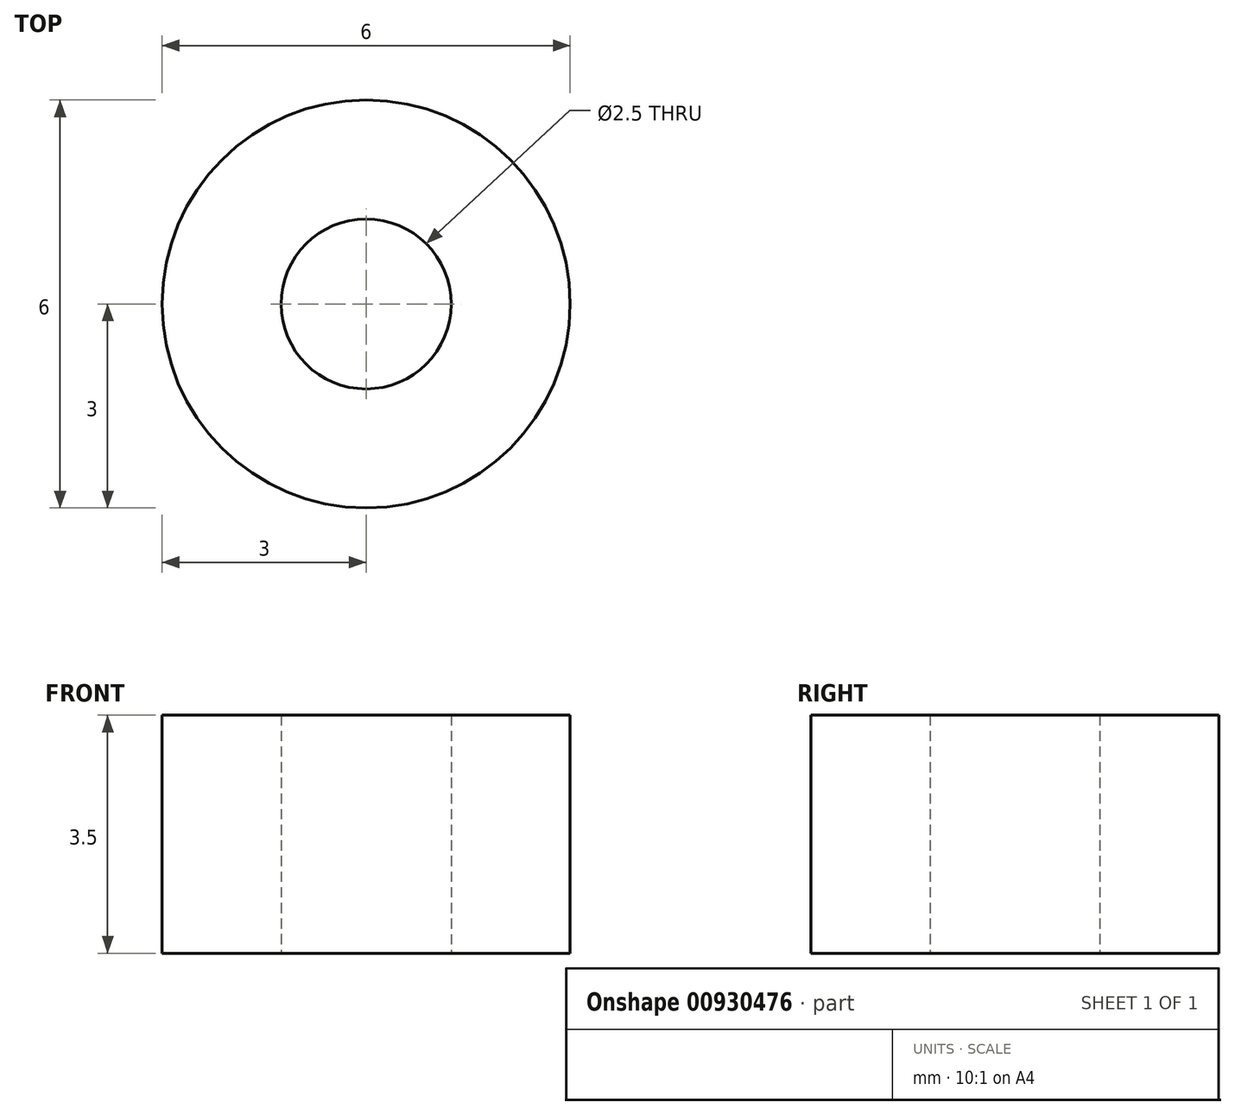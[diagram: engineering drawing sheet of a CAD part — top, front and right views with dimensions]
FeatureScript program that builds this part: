
annotation { "Feature Type Name" : "Feature", "Feature Type Description" : "" }
export const myFeature = defineFeature(function(context is Context, id is Id, definition is map)
    precondition{}
    {
        {
            var Q0;
            Q0=qCreatedBy(makeId("Top.planeOp"),FACE);
            var sketch = newSketch(context, id + "F0", { "sketchPlane" : qUnion([Q0])});
            skCircle(sketch, "E0", {"center": v(0, 0) * mm, "radius": 3 * mm});
            skCircle(sketch, "E1", {"center": v(0, 0) * mm, "radius": 1.25 * mm});
            skSolve(sketch);
        }
        {
            var Q0;
            Q0 = qSketchRegion(id + "F0", true);
            extrude(context, id + "F1", {"entities" : qUnion([Q0]), "depth" : 3.5 * mm, "offsetDistance" : 25 * mm});
        }
    });
